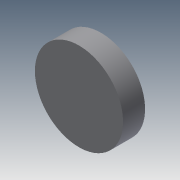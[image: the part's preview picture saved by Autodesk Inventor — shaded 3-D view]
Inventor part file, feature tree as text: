
AUTODESK INVENTOR PART (.ipt)
format: ipt  version: 2013 (Build 170138000, 138)  size: 70,656 bytes
history: native  units: mm
features: extrude x1, sketch x1
ambient origin geometry x8: Origin, YZ Plane, XZ Plane, XY Plane, X Axis, Y Axis, Z Axis, Center Point
bodies: Solid1 (feature_tree)
feature tree (2):
  extrude  "Extrusion1"  Depth=1.5mm TaperAngle=0.0deg
  sketch  "Sketch1"  dims[d0=6.0mm d1=1.5mm d2=0.0mm]
